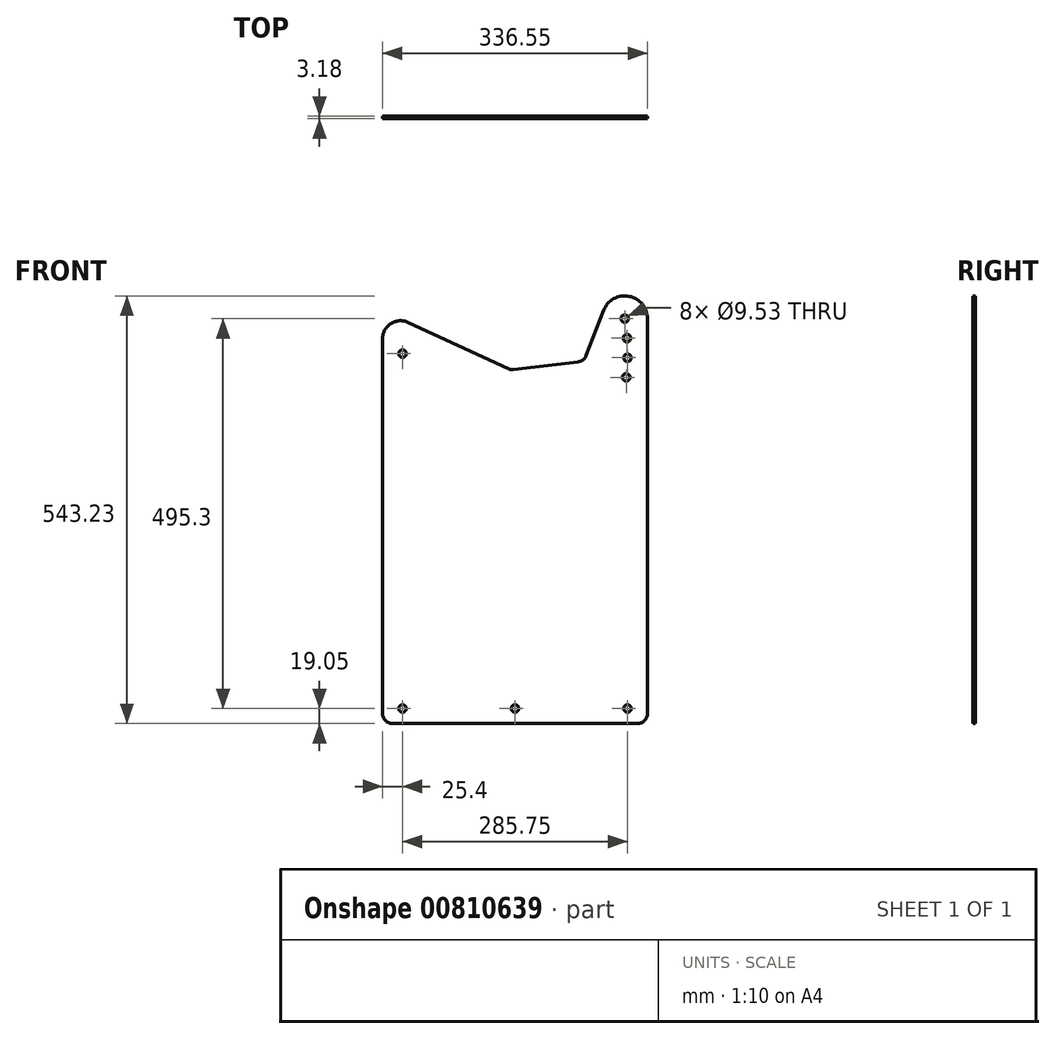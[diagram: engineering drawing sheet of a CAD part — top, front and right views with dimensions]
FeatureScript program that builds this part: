
annotation { "Feature Type Name" : "Feature", "Feature Type Description" : "" }
export const myFeature = defineFeature(function(context is Context, id is Id, definition is map)
    precondition{}
    {
        {
            var Q0;
            Q0=qCreatedBy(makeId("Front.planeOp"),FACE);
            var sketch = newSketch(context, id + "F0", { "sketchPlane" : qUnion([Q0])});
            skLineSegment(sketch, "E0", {"start": v(0, 0) * mm, "end": v(790, 0) * mm});
            skSolve(sketch);
        }
        {
            var Q0;
            Q0=qCreatedBy(makeId("Front.planeOp"),FACE);
            var sketch = newSketch(context, id + "F1", { "sketchPlane" : qUnion([Q0])});
            skLineSegment(sketch, "E1.bottom", {"start": v(0, 0) * mm, "end": v(336.55, 0) * mm});
            skLineSegment(sketch, "E1.top", {"start": v(0, 508) * mm, "end": v(336.55, 508) * mm, "construction": true});
            skLineSegment(sketch, "E1.left", {"start": v(0, 0) * mm, "end": v(0, 508) * mm});
            skLineSegment(sketch, "E1.right", {"start": v(336.55, 0) * mm, "end": v(336.55, 508) * mm});
            skCircle(sketch, "E2", {"center": v(25.4, 419.1) * mm, "radius": 4.76 * mm});
            skCircle(sketch, "E3", {"center": v(307.67, 463.55) * mm, "radius": 4.76 * mm});
            skCircle(sketch, "E4", {"center": v(25.4, 419.1) * mm, "radius": 285.75 * mm, "construction": true});
            skCircle(sketch, "E5", {"center": v(310.47, 438.78) * mm, "radius": 4.76 * mm});
            skCircle(sketch, "E6", {"center": v(311.1, 413.86) * mm, "radius": 4.76 * mm});
            skCircle(sketch, "E7", {"center": v(309.56, 388.98) * mm, "radius": 4.76 * mm});
            skLineSegment(sketch, "E8", {"start": v(25.4, 419.1) * mm, "end": v(307.67, 463.55) * mm, "construction": true});
            skLineSegment(sketch, "E9", {"start": v(25.4, 419.1) * mm, "end": v(310.47, 438.78) * mm, "construction": true});
            skLineSegment(sketch, "E10", {"start": v(25.4, 419.1) * mm, "end": v(311.1, 413.86) * mm, "construction": true});
            skLineSegment(sketch, "E11", {"start": v(25.4, 419.1) * mm, "end": v(309.56, 388.98) * mm, "construction": true});
            skLineSegment(sketch, "E12", {"start": v(255.8, 409.53) * mm, "end": v(166.35, 398.86) * mm});
            skLineSegment(sketch, "E13", {"start": v(159.51, 399.95) * mm, "end": v(32.46, 458.77) * mm});
            skPoint(sketch, "E14.visualSharp", {"position": v(0, 473.8) * mm});
            skArc(sketch, "E14.filletArc", {"start": v(32.46, 458.77) * mm, "mid": v(10.55, 457.29) * mm, "end": v(0, 438.03) * mm});
            skPoint(sketch, "E15.visualSharp", {"position": v(349.88, 465.88) * mm});
            skPoint(sketch, "E16.visualSharp", {"position": v(162.78, 398.44) * mm});
            skPoint(sketch, "E17.visualSharp", {"position": v(255.8, 409.53) * mm});
            skArc(sketch, "E18", {"start": v(336.55, 463.55) * mm, "mid": v(312.97, 491.94) * mm, "end": v(280.74, 473.97) * mm});
            skLineSegment(sketch, "E19", {"start": v(255.8, 409.53) * mm, "end": v(280.74, 473.97) * mm});
            skLineSegment(sketch, "E20", {"start": v(159.51, 399.95) * mm, "end": v(162.78, 398.44) * mm});
            skLineSegment(sketch, "E21", {"start": v(166.35, 398.86) * mm, "end": v(162.78, 398.44) * mm});
            skSolve(sketch);
        }
        {
            var Q0;
            {var subQ0=sQuery(id+"F1.wireOp",EDGE,"E1.bottom");Q0=makeQuery(id+"F1.imprint","IMPRINT",FACE,{"disambiguationData":[TD([[makeQuery(id+"F1.imprint","IMPRINT",EDGE,{"derivedFrom":subQ0}),1.0]])]});}
            extrude(context, id + "F2", {"entities" : qUnion([Q0]), "depth" : 3.17 * mm, "offsetDistance" : 25.4 * mm});
        }
        {
            var Q0;
            Q0=makeQuery(id+"F2.opExtrude","SWEPT_EDGE",EDGE,{"disambiguationData":[OSD([sQuery(id+"F1.wireOp",EDGE,"E20"),sQuery(id+"F1.wireOp",EDGE,"E21")])]});
            var Q1;
            Q1=makeQuery(id+"F2.opExtrude","SWEPT_EDGE",EDGE,{"disambiguationData":[OSD([sQuery(id+"F1.wireOp",EDGE,"E12"),sQuery(id+"F1.wireOp",EDGE,"E19")])]});
            fillet(context, id + "F3", {"entities" : qUnion([Q0, Q1]), "radius" : 12.7 * mm, "tangentPropagation" : true, "allowEdgeOverflow" : false});
        }
        {
            var Q0;
            Q0=makeQuery(id+"F2.opExtrude","SWEPT_FACE",FACE,{"disambiguationData":[OSD([sQuery(id+"F1.wireOp",EDGE,"E1.bottom")])]});
            extrude(context, id + "F4", {"entities" : qUnion([Q0]), "operationType" : NewBodyOperationType.ADD, "depth" : 50.8 * mm, "offsetDistance" : 25.4 * mm});
        }
        {
            var Q0;
            Q0=makeQuery(id+"F4.opExtrude","CAP_EDGE",EDGE,{"disambiguationData":[OSD([sQuery(id+"F1.wireOp",EDGE,"E1.bottom"),sQuery(id+"F1.wireOp",EDGE,"E1.left")])],"isStart":false});
            var Q1;
            Q1=makeQuery(id+"F4.opExtrude","CAP_EDGE",EDGE,{"disambiguationData":[OSD([sQuery(id+"F1.wireOp",EDGE,"E1.bottom"),sQuery(id+"F1.wireOp",EDGE,"E1.right")])],"isStart":false});
            fillet(context, id + "F5", {"entities" : qUnion([Q0, Q1]), "radius" : 12.7 * mm, "tangentPropagation" : true, "allowEdgeOverflow" : false});
        }
        {
            var Q0;
            {var subQ0=sQuery(id+"F1.wireOp",EDGE,"E1.bottom");Q0=makeQuery(id+"F4.boolean.opBoolean","MERGE",FACE,{"derivedFrom":[makeQuery(id+"F2.opExtrude","CAP_FACE",FACE,{"disambiguationData":[OSD([subQ0,sQuery(id+"F1.wireOp",EDGE,"E1.left"),sQuery(id+"F1.wireOp",EDGE,"E1.right"),sQuery(id+"F1.wireOp",EDGE,"E2"),sQuery(id+"F1.wireOp",EDGE,"E3"),sQuery(id+"F1.wireOp",EDGE,"E5"),sQuery(id+"F1.wireOp",EDGE,"E6"),sQuery(id+"F1.wireOp",EDGE,"E7"),sQuery(id+"F1.wireOp",EDGE,"E12"),sQuery(id+"F1.wireOp",EDGE,"E13"),sQuery(id+"F1.wireOp",EDGE,"E14.filletArc"),sQuery(id+"F1.wireOp",EDGE,"E18"),sQuery(id+"F1.wireOp",EDGE,"E19"),sQuery(id+"F1.wireOp",EDGE,"E20"),sQuery(id+"F1.wireOp",EDGE,"E21")])],"isStart":false}),makeQuery(id+"F4.opExtrude","SWEPT_FACE",FACE,{"disambiguationData":[OSD([subQ0]),TDD([makeQuery(id+"F2.opExtrude","CAP_EDGE",EDGE,{"disambiguationData":[OSD([subQ0])],"isStart":false})])]})]});}
            var sketch = newSketch(context, id + "F6", { "sketchPlane" : qUnion([Q0])});
            skCircle(sketch, "E22", {"center": v(25.4, -31.75) * mm, "radius": 4.76 * mm});
            skCircle(sketch, "E23", {"center": v(168.28, -31.75) * mm, "radius": 4.76 * mm});
            skCircle(sketch, "E24", {"center": v(311.15, -31.75) * mm, "radius": 4.76 * mm});
            skLineSegment(sketch, "E25", {"start": v(25.4, -31.75) * mm, "end": v(311.15, -31.75) * mm, "construction": true});
            skSolve(sketch);
        }
        {
            var Q0;
            Q0=makeQuery(id+"F6.imprint","IMPRINT",FACE,{"disambiguationData":[TD([[makeQuery(id+"F6.imprint","IMPRINT",EDGE,{"derivedFrom":sQuery(id+"F6.wireOp",EDGE,"E22")}),1.0]])]});
            var Q1;
            Q1=makeQuery(id+"F6.imprint","IMPRINT",FACE,{"disambiguationData":[TD([[makeQuery(id+"F6.imprint","IMPRINT",EDGE,{"derivedFrom":sQuery(id+"F6.wireOp",EDGE,"E23")}),1.0]])]});
            var Q2;
            Q2=makeQuery(id+"F6.imprint","IMPRINT",FACE,{"disambiguationData":[TD([[makeQuery(id+"F6.imprint","IMPRINT",EDGE,{"derivedFrom":sQuery(id+"F6.wireOp",EDGE,"E24")}),1.0]])]});
            extrude(context, id + "F7", {"entities" : qUnion([Q0, Q1, Q2]), "operationType" : NewBodyOperationType.REMOVE, "endBound" : BoundingType.THROUGH_ALL, "oppositeDirection" : true, "depth" : 25.4 * mm, "offsetDistance" : 25.4 * mm});
        }
    });
